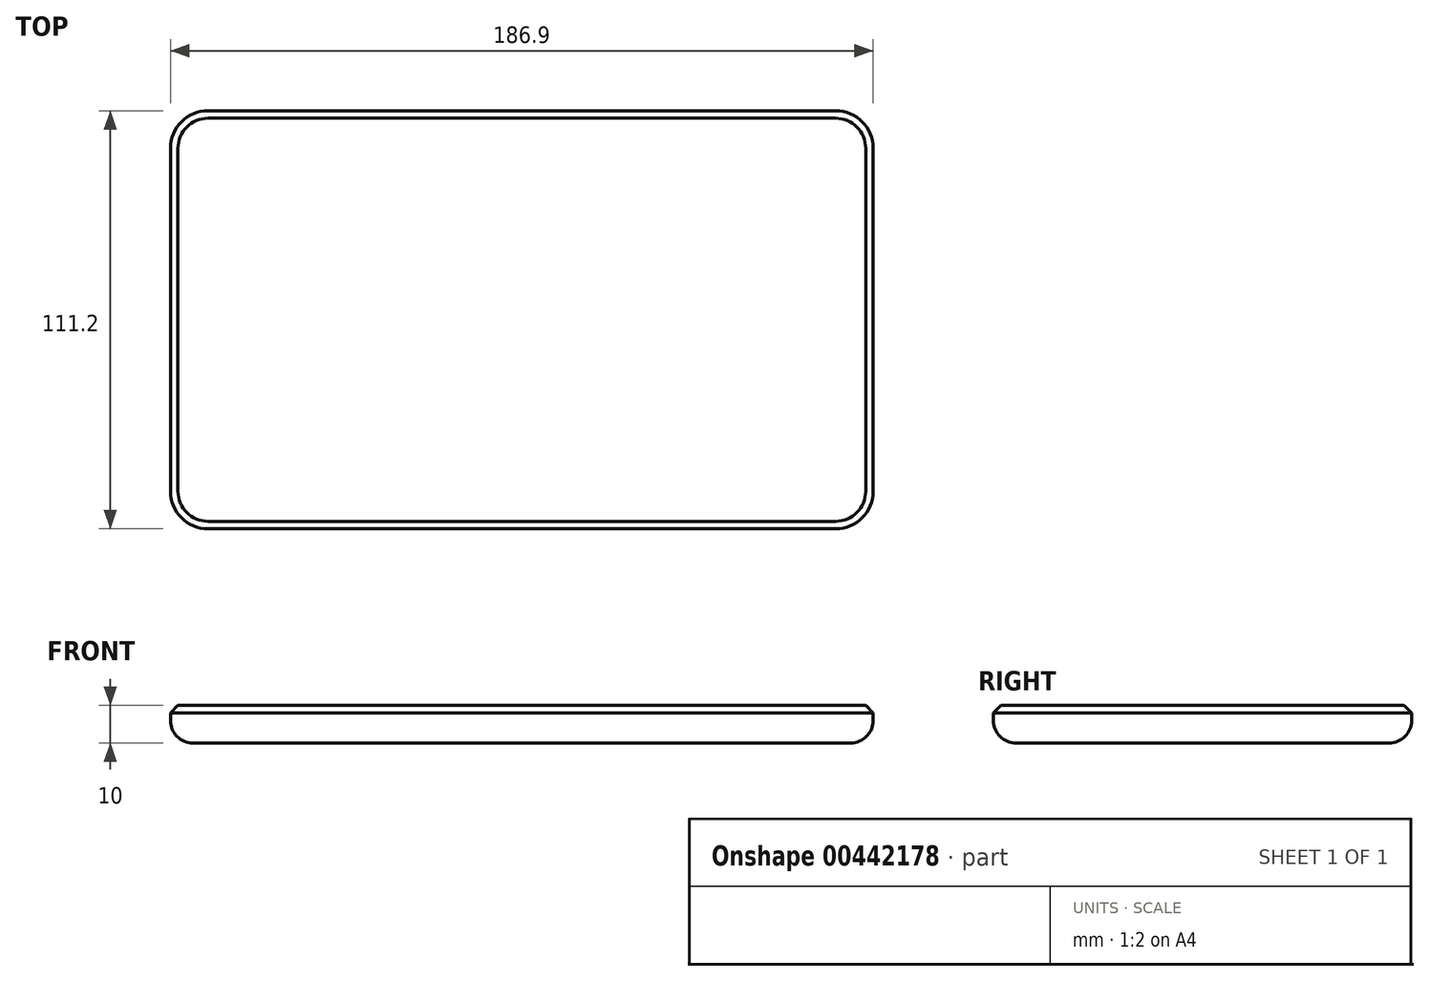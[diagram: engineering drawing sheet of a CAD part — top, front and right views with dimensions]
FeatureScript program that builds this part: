
annotation { "Feature Type Name" : "Feature", "Feature Type Description" : "" }
export const myFeature = defineFeature(function(context is Context, id is Id, definition is map)
    precondition{}
    {
        {
            var Q0;
            Q0=qCreatedBy(makeId("Top.planeOp"),FACE);
            var sketch = newSketch(context, id + "F0", { "sketchPlane" : qUnion([Q0])});
            skLineSegment(sketch, "E0.bottom", {"start": v(93.45, -55.6) * mm, "end": v(-93.45, -55.6) * mm});
            skLineSegment(sketch, "E0.top", {"start": v(93.45, 55.6) * mm, "end": v(-93.45, 55.6) * mm});
            skLineSegment(sketch, "E0.left", {"start": v(93.45, -55.6) * mm, "end": v(93.45, 55.6) * mm});
            skLineSegment(sketch, "E0.right", {"start": v(-93.45, -55.6) * mm, "end": v(-93.45, 55.6) * mm});
            skPoint(sketch, "E0.middle", {"position": v(0, 0) * mm});
            skSolve(sketch);
        }
        {
            var Q0;
            Q0=makeQuery(id+"F0.imprint","IMPRINT",FACE,{"disambiguationData":[TD([[makeQuery(id+"F0.imprint","IMPRINT",EDGE,{"derivedFrom":sQuery(id+"F0.wireOp",EDGE,"E0.bottom")}),-1.0]])]});
            extrude(context, id + "F1", {"entities" : qUnion([Q0]), "depth" : 10 * mm});
        }
        {
            var Q0;
            Q0=makeQuery(id+"F1.opExtrude","SWEPT_EDGE",EDGE,{"disambiguationData":[OSD([sQuery(id+"F0.wireOp",EDGE,"E0.top"),sQuery(id+"F0.wireOp",EDGE,"E0.left")])]});
            var Q1;
            Q1=makeQuery(id+"F1.opExtrude","SWEPT_EDGE",EDGE,{"disambiguationData":[OSD([sQuery(id+"F0.wireOp",EDGE,"E0.bottom"),sQuery(id+"F0.wireOp",EDGE,"E0.left")])]});
            var Q2;
            Q2=makeQuery(id+"F1.opExtrude","SWEPT_EDGE",EDGE,{"disambiguationData":[OSD([sQuery(id+"F0.wireOp",EDGE,"E0.top"),sQuery(id+"F0.wireOp",EDGE,"E0.right")])]});
            var Q3;
            Q3=makeQuery(id+"F1.opExtrude","SWEPT_EDGE",EDGE,{"disambiguationData":[OSD([sQuery(id+"F0.wireOp",EDGE,"E0.bottom"),sQuery(id+"F0.wireOp",EDGE,"E0.right")])]});
            fillet(context, id + "F2", {"entities" : qUnion([Q0, Q1, Q2, Q3]), "radius" : 10 * mm, "tangentPropagation" : true, "allowEdgeOverflow" : false});
        }
        {
            var Q0;
            Q0=makeQuery(id+"F1.opExtrude","CAP_EDGE",EDGE,{"disambiguationData":[OSD([sQuery(id+"F0.wireOp",EDGE,"E0.top")])],"isStart":false});
            chamfer(context, id + "F3", {"entities" : qUnion([Q0]), "width" : 2 * mm, "tangentPropagation" : true});
        }
        {
            var Q0;
            Q0=makeQuery(id+"F1.opExtrude","CAP_EDGE",EDGE,{"disambiguationData":[OSD([sQuery(id+"F0.wireOp",EDGE,"E0.top")])],"isStart":true});
            fillet(context, id + "F4", {"entities" : qUnion([Q0]), "radius" : 6 * mm, "tangentPropagation" : true, "allowEdgeOverflow" : false});
        }
    });
